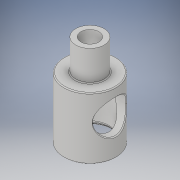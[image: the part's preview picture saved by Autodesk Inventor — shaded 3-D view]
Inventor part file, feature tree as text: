
AUTODESK INVENTOR PART (.ipt)
format: ipt  version: 2018 (Build 220112000, 112)  size: 213,504 bytes
history: native  units: mm
features: sketch x2, revolve x1, extrude x1, chamfer x1
ambient origin geometry x8: Origin, YZ Plane, XZ Plane, XY Plane, X Axis, Y Axis, Z Axis, Center Point
bodies: Solid1 (feature_tree)
feature tree (5):
  revolve  "Revolution1"  [1 undecoded]
  extrude  "Extrusion1"  TaperAngle=45.0deg  [1 undecoded]
  chamfer  "Chamfer1"  Distance=0.74mm
  sketch  "Sketch1"  dims[d0=13.05mm d1=6.4mm]
  sketch  "Sketch2"  dims[d2=11.05mm d3=45.0deg d4=0.74mm d5=1.9mm d6=3.0mm d7=4.0mm d8=5.5mm d9=0.2mm d10=0.2mm d11=0.5mm d12=0.22mm d13=90.0deg d14=7.0mm d15=7.55mm d16=10.0mm d17=0.0mm d18=0.2mm d19=2.0mm d20=45.0deg d21=0.2mm]
note: 2 required parameter values undecoded (feature->parameter linkage not recoverable at this tier; creation-order binding heuristic only, values carry confidence <= 0.55)